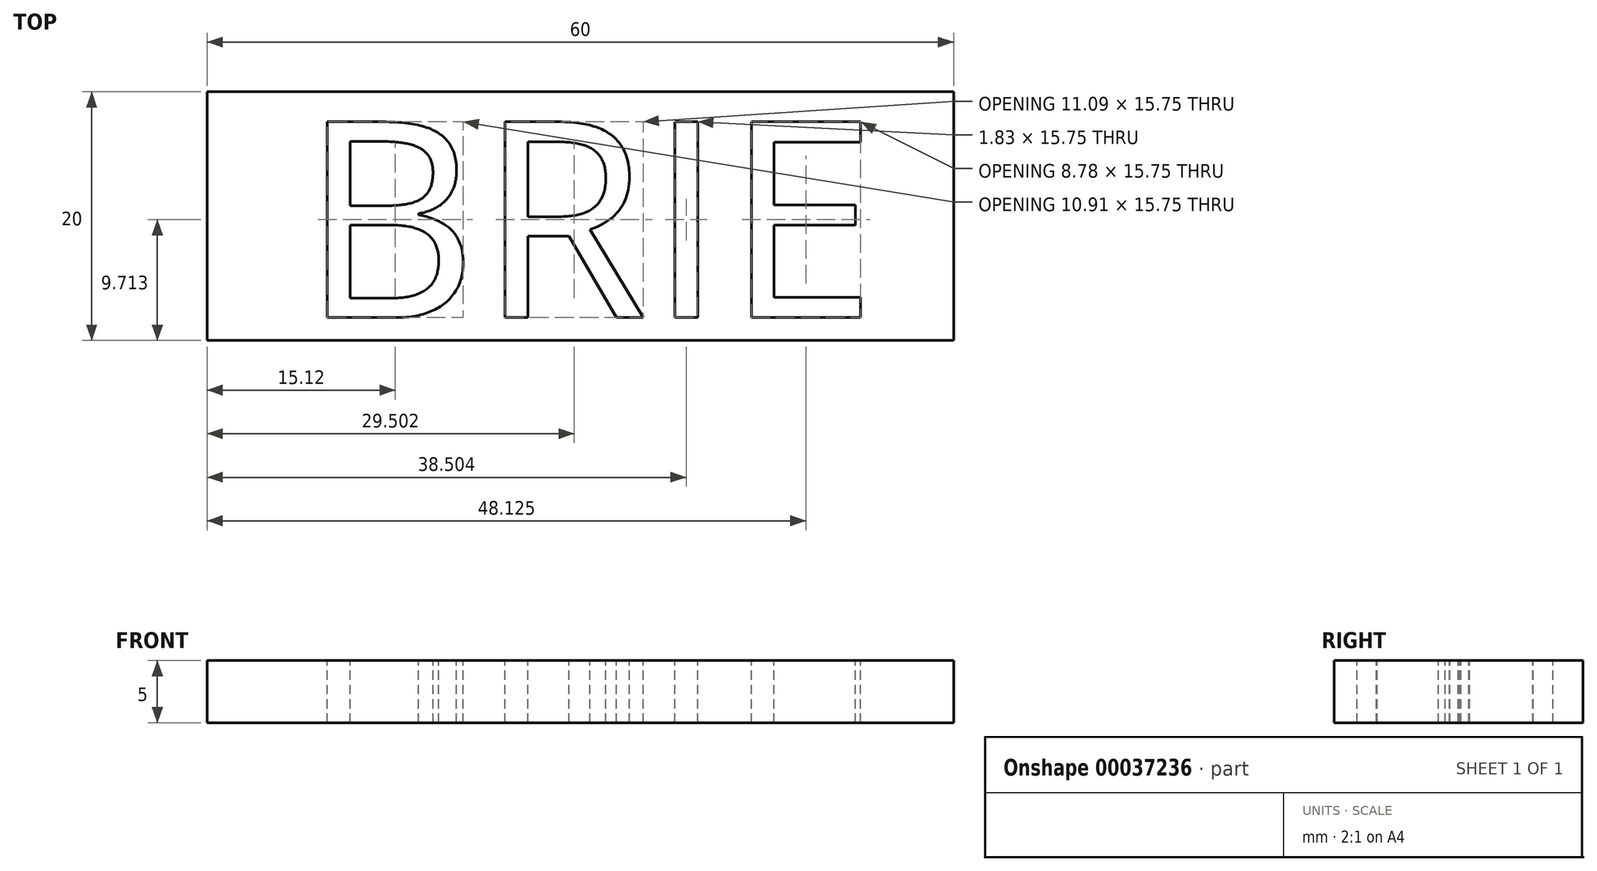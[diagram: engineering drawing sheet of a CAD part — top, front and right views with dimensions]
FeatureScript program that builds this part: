
annotation { "Feature Type Name" : "Feature", "Feature Type Description" : "" }
export const myFeature = defineFeature(function(context is Context, id is Id, definition is map)
    precondition{}
    {
        {
            var Q0;
            Q0=qCreatedBy(makeId("Top.planeOp"),FACE);
            var sketch = newSketch(context, id + "F0", { "sketchPlane" : qUnion([Q0])});
            skLineSegment(sketch, "E0.rect.bottom", {"start": v(30, -10) * mm, "end": v(-30, -10) * mm});
            skLineSegment(sketch, "E0.rect.top", {"start": v(30, 10) * mm, "end": v(-30, 10) * mm});
            skLineSegment(sketch, "E0.rect.left", {"start": v(30, -10) * mm, "end": v(30, 10) * mm});
            skLineSegment(sketch, "E0.rect.right", {"start": v(-30, -10) * mm, "end": v(-30, 10) * mm});
            skPoint(sketch, "E0.rect.middle", {"position": v(0, 0) * mm});
            skSolve(sketch);
        }
        {
            var Q0;
            Q0=makeQuery(id+"F0.imprint","IMPRINT",FACE,{"disambiguationData":[TD([[makeQuery(id+"F0.imprint","IMPRINT",EDGE,{"derivedFrom":sQuery(id+"F0.wireOp",EDGE,"E0.rect.bottom")}),-1.0]])]});
            extrude(context, id + "F1", {"entities" : qUnion([Q0]), "depth" : 5 * mm});
        }
        {
            var Q0;
            Q0=makeQuery(id+"F1.opExtrude","CAP_FACE",FACE,{"disambiguationData":[OSD([sQuery(id+"F0.wireOp",EDGE,"E0.rect.bottom"),sQuery(id+"F0.wireOp",EDGE,"E0.rect.top"),sQuery(id+"F0.wireOp",EDGE,"E0.rect.left"),sQuery(id+"F0.wireOp",EDGE,"E0.rect.right")])],"isStart":false});
            var sketch = newSketch(context, id + "F2", { "sketchPlane" : qUnion([Q0])});
            skText(sketch, "E1", { "text": "BRIE", "fontName": "OpenSans-Regular.ttf"});
            const initialGuessF2  = {"E1": [-0.0225, -0.00816, 1, 0, 0.01588]};
            skSetInitialGuess(sketch, initialGuessF2);
            skSolve(sketch);
        }
        {
            var Q0;
            Q0 = qSketchRegion(id + "F2", true);
            extrude(context, id + "F3", {"entities" : qUnion([Q0]), "operationType" : NewBodyOperationType.REMOVE, "endBound" : BoundingType.THROUGH_ALL, "oppositeDirection" : true, "depth" : 25 * mm});
        }
    });
